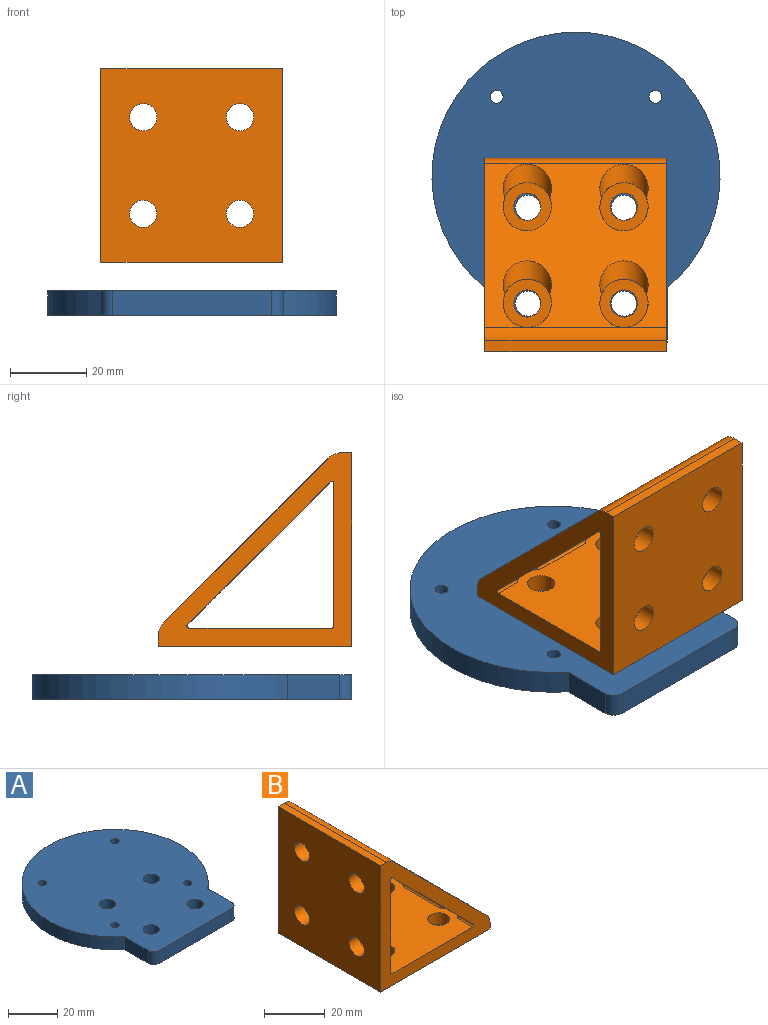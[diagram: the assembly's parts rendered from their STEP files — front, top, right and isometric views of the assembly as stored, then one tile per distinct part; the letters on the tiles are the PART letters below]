
ASSEMBLY  parts=2 mates=1
PART A: 16 faces, bbox 75.7x84x6.4 mm
  f0: plane 13.72x6.35mm, normal (1,0,0), area 87.1mm2, adj f1,f12,f14,f15
  f1: cylinder r=37.84mm len=75.69mm, axis (0,0,-1), area 1179.8mm2, adj f0,f2,f14,f15
  f2: plane 13.72x6.35mm, normal (-1,0,0), area 87.1mm2, adj f1,f3,f14,f15
  f3: cylinder r=3.17mm len=6.35mm, axis (0,0,-1), area 31.7mm2, adj f2,f4,f14,f15
  f4: plane 41.65x6.35mm, normal (0,-1,0), area 264.5mm2, adj f3,f12,f14,f15
  f5: cylinder r=3.3mm len=6.6mm, axis (0,0,-1), area 131.7mm2, adj f14,f15
  f6: cylinder r=1.7mm len=6.35mm, axis (0,0,-1), area 67.8mm2, adj f14,f15
  f7: cylinder r=1.7mm len=6.35mm, axis (0,0,-1), area 67.8mm2, adj f14,f15
  f8: cylinder r=1.7mm len=6.35mm, axis (0,0,-1), area 67.8mm2, adj f14,f15
  f9: cylinder r=1.7mm len=6.35mm, axis (0,0,-1), area 67.8mm2, adj f14,f15
  f10: cylinder r=3.3mm len=6.6mm, axis (0,0,-1), area 131.7mm2, adj f14,f15
  f11: cylinder r=3.3mm len=6.6mm, axis (0,0,-1), area 131.7mm2, adj f14,f15
  f12: cylinder r=3.17mm len=6.35mm, axis (0,0,-1), area 31.7mm2, adj f0,f4,f14,f15
  f13: cylinder r=3.3mm len=6.6mm, axis (0,0,-1), area 131.7mm2, adj f14,f15
  f14: plane 84x75.69mm, normal (0,0,1), area 4851.6mm2, adj f0,f1,f2,f3,f4,f5,f6,f7
  f15: plane 84x75.69mm, normal (0,0,-1), area 4851.6mm2, adj f0,f1,f2,f3,f4,f5,f6,f7
PART B: 43 faces, bbox 50.8x47.6x50.8 mm
  f0: cylinder r=6.35mm len=12.7mm, axis (-1,0,0), area 106.8mm2, adj f1,f18,f29
  f1: cylinder r=6.35mm len=12.7mm, axis (0,0,-1), area 106.8mm2, adj f0,f15,f29
  f2: cylinder r=6.35mm len=12.7mm, axis (-1,0,0), area 106.8mm2, adj f3,f20,f29
  f3: cylinder r=6.35mm len=12.7mm, axis (0,0,-1), area 106.8mm2, adj f2,f14,f29
  f4: cylinder r=6.35mm len=12.7mm, axis (-1,0,0), area 106.8mm2, adj f5,f11,f29
  f5: cylinder r=6.35mm len=12.7mm, axis (0,0,-1), area 106.8mm2, adj f4,f12,f29
  f6: cylinder r=6.35mm len=12.7mm, axis (-1,0,0), area 106.8mm2, adj f7,f8,f29
  f7: cylinder r=6.35mm len=12.7mm, axis (0,0,-1), area 106.8mm2, adj f6,f9,f29
  f8: cylinder r=6.35mm len=12.7mm, axis (0,0,-1), area 41.4mm2, adj f6,f9,f32
  f9: cylinder r=6.35mm len=12.7mm, axis (-1,0,0), area 41.4mm2, adj f7,f8,f10,f16,f31,f32
  f10: cylinder r=0.51mm len=18.19mm, axis (0,1,0), area 21.3mm2, adj f9,f12,f31,f32
  f11: cylinder r=6.35mm len=12.7mm, axis (0,0,-1), area 41.4mm2, adj f4,f12,f32
  f12: cylinder r=6.35mm len=12.7mm, axis (-1,0,0), area 41.4mm2, adj f5,f10,f11,f13,f31,f32
  f13: cylinder r=0.51mm len=7.51mm, axis (0,1,0), area 8.8mm2, adj f12,f31,f32,f41
  f14: cylinder r=6.35mm len=12.7mm, axis (-1,0,0), area 41.4mm2, adj f3,f20,f32
  f15: cylinder r=6.35mm len=12.7mm, axis (-1,0,0), area 41.4mm2, adj f1,f18,f32
  f16: cylinder r=0.51mm len=7.51mm, axis (0,1,0), area 8.8mm2, adj f9,f31,f32,f39
  f17: cylinder r=0.51mm len=7.51mm, axis (0,1,0), area 8.8mm2, adj f18,f32,f33,f39
  f18: cylinder r=6.35mm len=12.7mm, axis (0,0,-1), area 41.4mm2, adj f0,f15,f17,f19,f32,f33
  f19: cylinder r=0.51mm len=18.19mm, axis (0,1,0), area 21.3mm2, adj f18,f20,f32,f33
  f20: cylinder r=6.35mm len=12.7mm, axis (0,0,-1), area 41.4mm2, adj f2,f14,f19,f21,f32,f33
  f21: cylinder r=0.51mm len=7.51mm, axis (0,1,0), area 8.8mm2, adj f20,f32,f33,f41
  f22: cylinder r=0.51mm len=47.63mm, axis (0,1,0), area 38mm2, adj f31,f33,f39,f41
  f23: cylinder r=3.57mm len=7.14mm, axis (0,0,-1), area 107.1mm2, adj f33,f40
  f24: cylinder r=3.57mm len=7.14mm, axis (0,0,-1), area 107.1mm2, adj f33,f40
  f25: cylinder r=3.57mm len=7.14mm, axis (0,0,-1), area 107.1mm2, adj f33,f40
  f26: cylinder r=3.57mm len=7.14mm, axis (0,0,-1), area 107.1mm2, adj f33,f40
  f27: plane 47.63x2.8mm, normal (1,0,0), area 133.2mm2, adj f28,f39,f40,f41
  f28: cylinder r=4.78mm len=47.63mm, axis (0,1,0), area 178.6mm2, adj f27,f29,f39,f41
  f29: plane 47.63x43.23mm, normal (0.71,0,0.71), area 1860.1mm2, adj f0,f1,f2,f3,f4,f5,f6,f7
  f30: cylinder r=4.78mm len=47.63mm, axis (0,1,0), area 178.6mm2, adj f29,f38,f39,f41
  f31: plane 47.63x39.17mm, normal (1,0,0), area 1646.7mm2, adj f9,f10,f12,f13,f16,f22,f34,f35
  f32: plane 47.63x37.54mm, normal (-0.71,0,-0.71), area 1707.4mm2, adj f8,f9,f10,f11,f12,f13,f14,f15
  f33: plane 47.63x39.17mm, normal (0,0,1), area 1646.7mm2, adj f17,f18,f19,f20,f21,f22,f23,f24
  f34: cylinder r=3.57mm len=7.14mm, axis (-1,0,0), area 107.1mm2, adj f31,f42
  f35: cylinder r=3.57mm len=7.14mm, axis (-1,0,0), area 107.1mm2, adj f31,f42
  f36: cylinder r=3.57mm len=7.14mm, axis (-1,0,0), area 107.1mm2, adj f31,f42
  f37: cylinder r=3.57mm len=7.14mm, axis (-1,0,0), area 107.1mm2, adj f31,f42
  f38: plane 47.63x2.8mm, normal (0,0,1), area 133.2mm2, adj f30,f39,f41,f42
  f39: plane 50.8x50.8mm, normal (0,-1,0), area 750.1mm2, adj f16,f17,f22,f27,f28,f29,f30,f31
  f40: plane 50.8x47.63mm, normal (0,0,-1), area 2259.3mm2, adj f23,f24,f25,f26,f27,f39,f41,f42
  f41: plane 50.8x50.8mm, normal (0,1,0), area 750.1mm2, adj f13,f21,f22,f27,f28,f29,f30,f31
  f42: plane 50.8x47.63mm, normal (-1,0,0), area 2259.3mm2, adj f34,f35,f36,f37,f38,f39,f40,f41
PLACE A t=(-4.91,81.25,-18.34)mm fixed
PLACE B rot(axis=(0,0,1),90deg) t=(-5.01,35.09,-4.45)mm
MATE slider A.f11 <-> B.f7  axis (0,0,1) through (7.69,47.79,-11.99)mm
